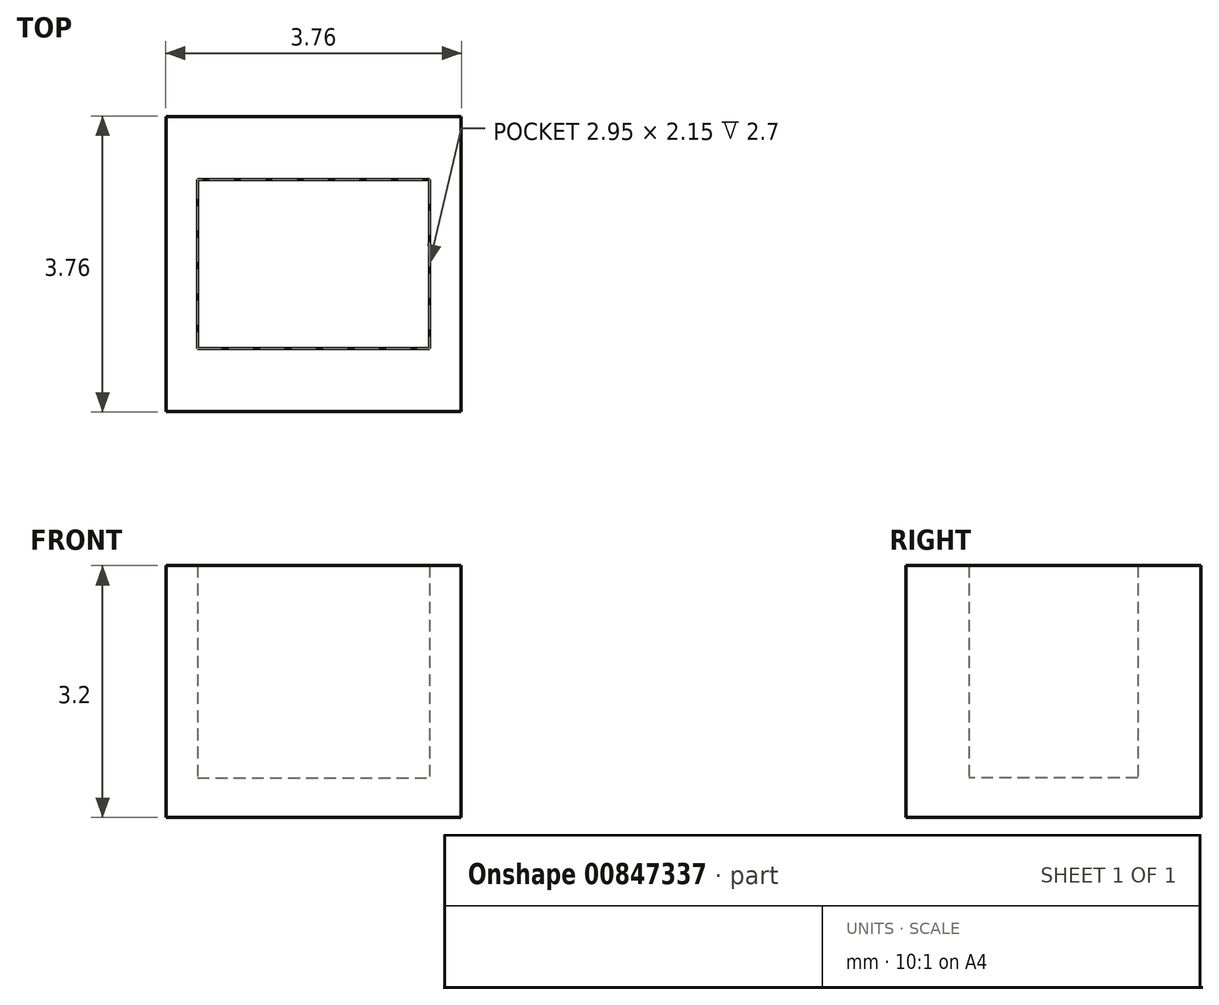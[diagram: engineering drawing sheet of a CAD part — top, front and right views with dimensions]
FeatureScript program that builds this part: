
annotation { "Feature Type Name" : "Feature", "Feature Type Description" : "" }
export const myFeature = defineFeature(function(context is Context, id is Id, definition is map)
    precondition{}
    {
        {
            var Q0;
            Q0=qCreatedBy(makeId("Top.planeOp"),FACE);
            var sketch = newSketch(context, id + "F0", { "sketchPlane" : qUnion([Q0])});
            skLineSegment(sketch, "E0.bottom", {"start": v(-1.87, 1.88) * mm, "end": v(1.88, 1.88) * mm});
            skLineSegment(sketch, "E0.top", {"start": v(-1.88, -1.88) * mm, "end": v(1.87, -1.88) * mm});
            skLineSegment(sketch, "E0.left", {"start": v(-1.87, 1.88) * mm, "end": v(-1.88, -1.88) * mm});
            skLineSegment(sketch, "E0.right", {"start": v(1.88, 1.88) * mm, "end": v(1.87, -1.88) * mm});
            skPoint(sketch, "E0.middle", {"position": v(0, 0) * mm});
            skLineSegment(sketch, "E1.bottom", {"start": v(-1.47, 1.07) * mm, "end": v(1.48, 1.07) * mm});
            skLineSegment(sketch, "E1.top", {"start": v(-1.48, -1.07) * mm, "end": v(1.47, -1.07) * mm});
            skLineSegment(sketch, "E1.left", {"start": v(-1.47, 1.07) * mm, "end": v(-1.48, -1.07) * mm});
            skLineSegment(sketch, "E1.right", {"start": v(1.48, 1.07) * mm, "end": v(1.47, -1.07) * mm});
            skSolve(sketch);
        }
        {
            var Q0;
            Q0 = qSketchRegion(id + "F0", true);
            var Q1;
            Q1=makeQuery(id+"F0.imprint","IMPRINT",FACE,{"disambiguationData":[TD([[makeQuery(id+"F0.imprint","IMPRINT",EDGE,{"derivedFrom":sQuery(id+"F0.wireOp",EDGE,"E0.bottom")}),-1.0]])]});
            extrude(context, id + "F1", {"entities" : qUnion([Q0, Q1]), "depth" : 3.2 * mm, "offsetDistance" : 25 * mm});
        }
        {
            var Q0;
            Q0=makeQuery(id+"F0.imprint","IMPRINT",FACE,{"disambiguationData":[TD([[makeQuery(id+"F0.imprint","IMPRINT",EDGE,{"derivedFrom":sQuery(id+"F0.wireOp",EDGE,"E1.bottom")}),-1.0]])]});
            extrude(context, id + "F2", {"entities" : qUnion([Q0]), "operationType" : NewBodyOperationType.ADD, "depth" : .5 * mm, "offsetDistance" : 25 * mm});
        }
    });
